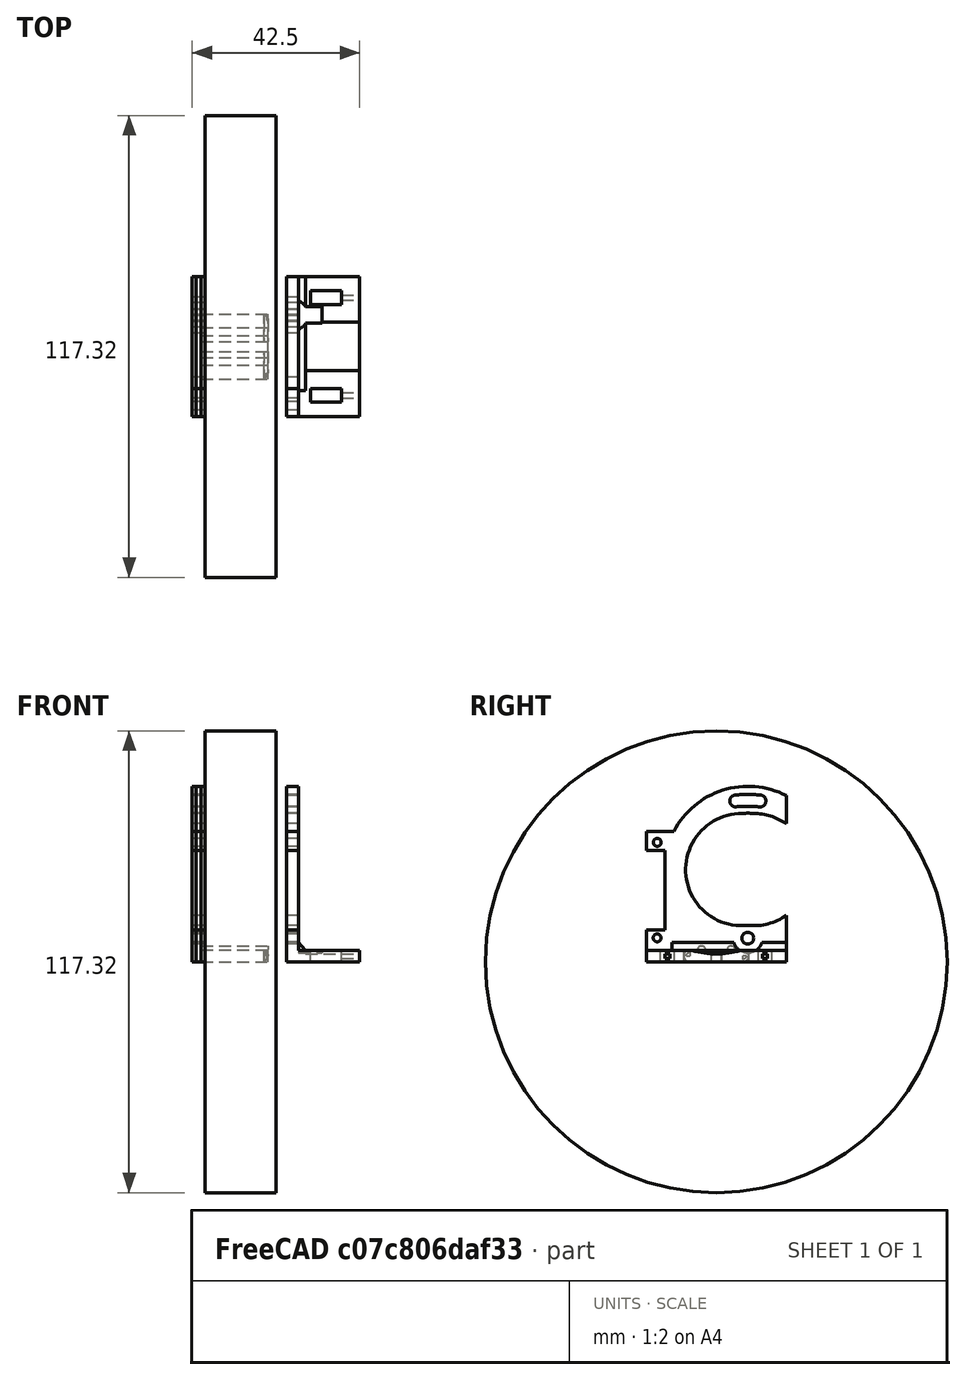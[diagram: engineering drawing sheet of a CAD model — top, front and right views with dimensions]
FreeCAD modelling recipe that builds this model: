
FCSTD DOCUMENT  (FreeCAD 0.20R29410 (Git))
Label: druk_backup
License: All rights reserved
LicenseURL: http://en.wikipedia.org/wiki/All_rights_reserved
objects: Part::Fillet×10, Part::Box×6, Part::FeaturePython×5, Part::Feature×2, Part::Chamfer×2, Part::Compound2×1, Sketcher::SketchObject×1, PartDesign::Pad×1, PartDesign::Body×1, App::DocumentObjectGroup×1, Part::Compound×1
note: 30 computed .brp shape members not serialized (recipe doc carries the construction recipe); baked Part::Feature solids carry a one-line shape summary decoded from their .brp

FEATURE [Part::Feature] Solid
  shape: bbox 18.5 x 35.5 x 44.6 mm, 50 faces (baked)
FEATURE [Part::Compound2] Compound  label="blinds mount v12"
  Links = -> [Solid]
  Placement = pos=(-23,0,0) rot=(0,0,1;0rad)
FEATURE [Sketcher::SketchObject] Sketch
  FullyConstrained = false
  MapMode = 5
  Placement = pos=(0,0,0) rot=(0.57735,0.57735,0.57735;2.0944rad)
  Support = -> [YZ_Plane]
  sketch-geometry (1):
    g0: Circle CenterX=0 CenterY=0 CenterZ=0 NormalX=0 NormalY=0 NormalZ=1 AngleXU=0 Radius=58.6601
  constraints (1):
    c: Coincident(g0,g-1)
FEATURE [PartDesign::Pad] Pad
  Direction = (1,-2e-16,3e-16)
  Length = 18
  Length2 = 10
  Placement = pos=(0,0,0) rot=(0.57735,0.57735,0.57735;2.0944rad)
  Profile = -> Sketch
  ReferenceAxis = -> Sketch [N_Axis]
  Type = 0
FEATURE [PartDesign::Body] Body
  Group = -> [Sketch,Pad]
  Origin = -> Origin
  Placement = pos=(-30,0,0) rot=(0,0,1;0rad)
  Tip = -> Pad
FEATURE [Part::FeaturePython] Slice  # WARN: FeaturePython — macro-defined, semantics opaque (R4)
  Base = -> Compound
  Mode = 1
  Tolerance = 0
  Tools = -> [Body,Solid]
FEATURE [Part::FeaturePython] Slice_child1  label="Slice.1"  # WARN: FeaturePython — macro-defined, semantics opaque (R4)
  Base = -> Slice
  FilterType = 1
  Invert = false
  OverrideMaxVal = 0
  WindowFrom = 80
  WindowTo = 100
  items = 1
FEATURE [App::DocumentObjectGroup] GrExplode_Slice  label="Exploded Slice"
  Group = -> [Slice_child1]
FEATURE [Part::Feature] Slice_child1001  label="Slice.002"
  Placement = pos=(-1,0,0) rot=(0,0,1;0rad)
  shape: bbox 2.25 x 35.5 x 44.6 mm, 24 faces (baked)
FEATURE [Part::Compound] Compound001
  Links = -> [GrExplode_Slice,Slice_child1001]
FEATURE [Part::Box] Box  label="Sześcian"
  AttacherType = Attacher::AttachEngine3D
  Height = 3
  Length = 17
  Placement = pos=(-31,-8.25,0) rot=(0,0,1;0rad)
  Width = 16.5
FEATURE [Part::Box] Box001  label="Sześcian001"
  AttacherType = Attacher::AttachEngine3D
  Height = 3
  Length = 17
  Placement = pos=(-31,-1.25,0) rot=(0,0,1;0rad)
  Width = 2.5
FEATURE [Part::FeaturePython] Slice001  # WARN: FeaturePython — macro-defined, semantics opaque (R4)
  Base = -> Box
  Mode = 1
  Tolerance = 0
  Tools = -> [Box001]
FEATURE [Part::Box] Box002  label="Sześcian002"
  AttacherType = Attacher::AttachEngine3D
  Height = 1
  Length = 17
  Placement = pos=(-31,-4.75,3) rot=(0,0,1;0rad)
  Width = 2
FEATURE [Part::Fillet] Fillet
  Base = -> Box002
  Edges = 1 edges r=0.9: [Edge10]
FEATURE [Part::Fillet] Fillet001
  Base = -> Fillet
  Edges = 1 edges r=0.9: [Edge14]
FEATURE [Part::Fillet] Fillet002
  Edges = 1 edges r=1.5: [Edge11]
FEATURE [Part::Fillet] Fillet003
  Base = -> Fillet002
  Edges = 1 edges r=1.49: [Edge14]
FEATURE [Part::Chamfer] Chamfer
  Base = -> Fillet003
  Edges = 1 edges r=1: [Edge8]
FEATURE [Part::Fillet] Fillet004
  Base = -> Chamfer
  Edges = 1 edges r=1.2: [Edge10]
FEATURE [Part::Box] Box004  label="Sześcian004"
  AttacherType = Attacher::AttachEngine3D
  Height = 3
  Length = 17
  Placement = pos=(-31,-8.25,0) rot=(0,0,1;0rad)
  Width = 16.5
FEATURE [Part::Box] Box005  label="Sześcian005"
  AttacherType = Attacher::AttachEngine3D
  Height = 3
  Length = 17
  Placement = pos=(-31,-1.25,0) rot=(0,0,1;0rad)
  Width = 2.5
FEATURE [Part::FeaturePython] Slice002  # WARN: FeaturePython — macro-defined, semantics opaque (R4)
  Base = -> Box004
  Mode = 1
  Tolerance = 0
  Tools = -> [Box005]
FEATURE [Part::FeaturePython] Slice001_child003  label="Slice001.003"  # WARN: FeaturePython — macro-defined, semantics opaque (R4)
  Base = -> Slice002
  FilterType = 1
  Invert = false
  OverrideMaxVal = 0
  WindowFrom = 80
  WindowTo = 100
  items = 0
FEATURE [Part::Fillet] Fillet005
  Base = -> Slice001_child003
  Edges = 1 edges r=1.5: [Edge11]
FEATURE [Part::Fillet] Fillet006
  Base = -> Fillet005
  Edges = 1 edges r=1.49: [Edge14]
FEATURE [Part::Chamfer] Chamfer001
  Base = -> Fillet006
  Edges = 1 edges r=1: [Edge8]
FEATURE [Part::Fillet] Fillet007
  Base = -> Chamfer001
  Edges = 1 edges r=1.2: [Edge10]
  Placement = pos=(0,0,3) rot=(1,0,0;3.14159rad)
FEATURE [Part::Box] Box006  label="Sześcian006"
  AttacherType = Attacher::AttachEngine3D
  Height = 1
  Length = 17
  Placement = pos=(-31,-4.75,3) rot=(0,0,1;0rad)
  Width = 2
FEATURE [Part::Fillet] Fillet008
  Base = -> Box006
  Edges = 1 edges r=0.9: [Edge10]
FEATURE [Part::Fillet] Fillet009
  Base = -> Fillet008
  Edges = 1 edges r=0.9: [Edge14]
  Placement = pos=(0,7.5,0) rot=(0,0,1;0rad)
